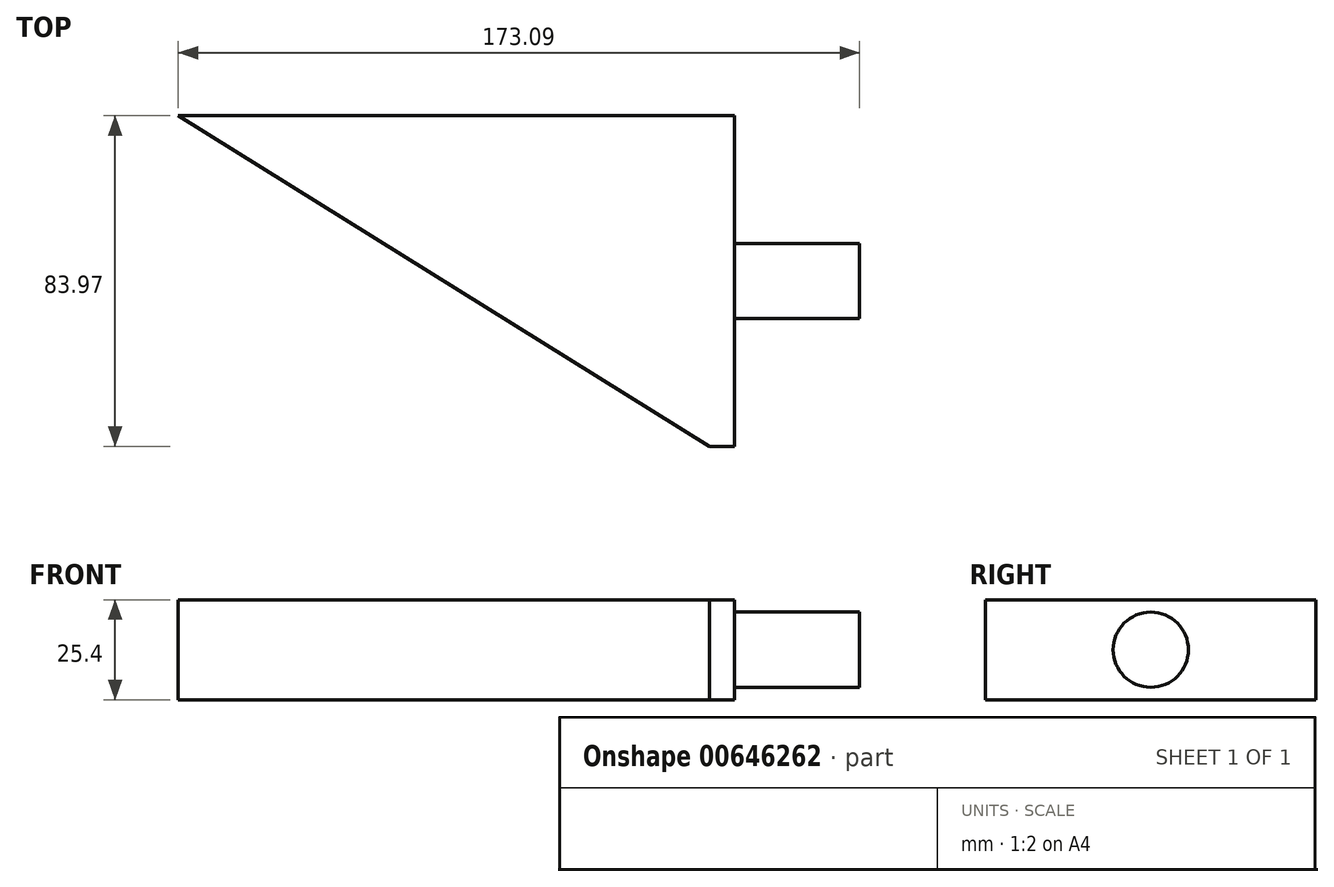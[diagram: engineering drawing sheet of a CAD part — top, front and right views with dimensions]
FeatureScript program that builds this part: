
annotation { "Feature Type Name" : "Feature", "Feature Type Description" : "" }
export const myFeature = defineFeature(function(context is Context, id is Id, definition is map)
    precondition{}
    {
        {
            var Q0;
            Q0=qCreatedBy(makeId("Top.planeOp"),FACE);
            var sketch = newSketch(context, id + "F0", { "sketchPlane" : qUnion([Q0])});
            skLineSegment(sketch, "E0", {"start": v(-67.34, 57.67) * mm, "end": v(67.65, 57.67) * mm});
            skLineSegment(sketch, "E1", {"start": v(67.65, 57.67) * mm, "end": v(67.65, -26.3) * mm});
            skLineSegment(sketch, "E2", {"start": v(67.65, -26.3) * mm, "end": v(-67.34, 57.67) * mm});
            skSolve(sketch);
        }
        {
            var Q0;
            Q0=makeQuery(id+"F0.imprint","IMPRINT",FACE,{"disambiguationData":[TD([[makeQuery(id+"F0.imprint","IMPRINT",EDGE,{"derivedFrom":sQuery(id+"F0.wireOp",EDGE,"E0")}),-1.0]])]});
            extrude(context, id + "F1", {"entities" : qUnion([Q0]), "depth" : 25.4 * mm, "offsetDistance" : 25.4 * mm});
        }
        {
            var Q0;
            Q0=makeQuery(id+"F1.opExtrude","SWEPT_FACE",FACE,{"disambiguationData":[OSD([sQuery(id+"F0.wireOp",EDGE,"E1")])]});
            var sketch = newSketch(context, id + "F2", { "sketchPlane" : qUnion([Q0])});
            skLineSegment(sketch, "E3.bottom", {"start": v(57.67, 0) * mm, "end": v(-26.3, 0) * mm});
            skLineSegment(sketch, "E3.top", {"start": v(57.67, 25.4) * mm, "end": v(-26.3, 25.4) * mm});
            skLineSegment(sketch, "E3.left", {"start": v(57.67, 0) * mm, "end": v(57.67, 25.4) * mm});
            skLineSegment(sketch, "E3.right", {"start": v(-26.3, 0) * mm, "end": v(-26.3, 25.4) * mm});
            skSolve(sketch);
        }
        {
            var Q0;
            Q0=makeQuery(id+"F2.imprint","IMPRINT",FACE,{"disambiguationData":[TD([[makeQuery(id+"F2.imprint","IMPRINT",EDGE,{"derivedFrom":sQuery(id+"F2.wireOp",EDGE,"E3.bottom")}),-1.0]])]});
            extrude(context, id + "F3", {"entities" : qUnion([Q0]), "operationType" : NewBodyOperationType.ADD, "depth" : 6.35 * mm, "offsetDistance" : 25.4 * mm});
        }
        {
            var Q0;
            Q0=makeQuery(id+"F3.opExtrude","CAP_FACE",FACE,{"disambiguationData":[OSD([sQuery(id+"F2.wireOp",EDGE,"E3.bottom"),sQuery(id+"F2.wireOp",EDGE,"E3.top"),sQuery(id+"F2.wireOp",EDGE,"E3.left"),sQuery(id+"F2.wireOp",EDGE,"E3.right")])],"isStart":false});
            var sketch = newSketch(context, id + "F4", { "sketchPlane" : qUnion([Q0])});
            skCircle(sketch, "E4", {"center": v(15.69, 12.7) * mm, "radius": 9.55 * mm});
            skPoint(sketch, "E4.centerSnap0", {"position": v(15.69, 25.4) * mm});
            skPoint(sketch, "E4.centerSnap1", {"position": v(-26.3, 12.7) * mm});
            skSolve(sketch);
        }
        {
            var Q0;
            Q0=makeQuery(id+"F4.imprint","IMPRINT",FACE,{"disambiguationData":[TD([[makeQuery(id+"F4.imprint","IMPRINT",EDGE,{"derivedFrom":sQuery(id+"F4.wireOp",EDGE,"E4")}),1.0]])]});
            extrude(context, id + "F5", {"entities" : qUnion([Q0]), "operationType" : NewBodyOperationType.ADD, "depth" : 31.75 * mm, "offsetDistance" : 25.4 * mm});
        }
    });
